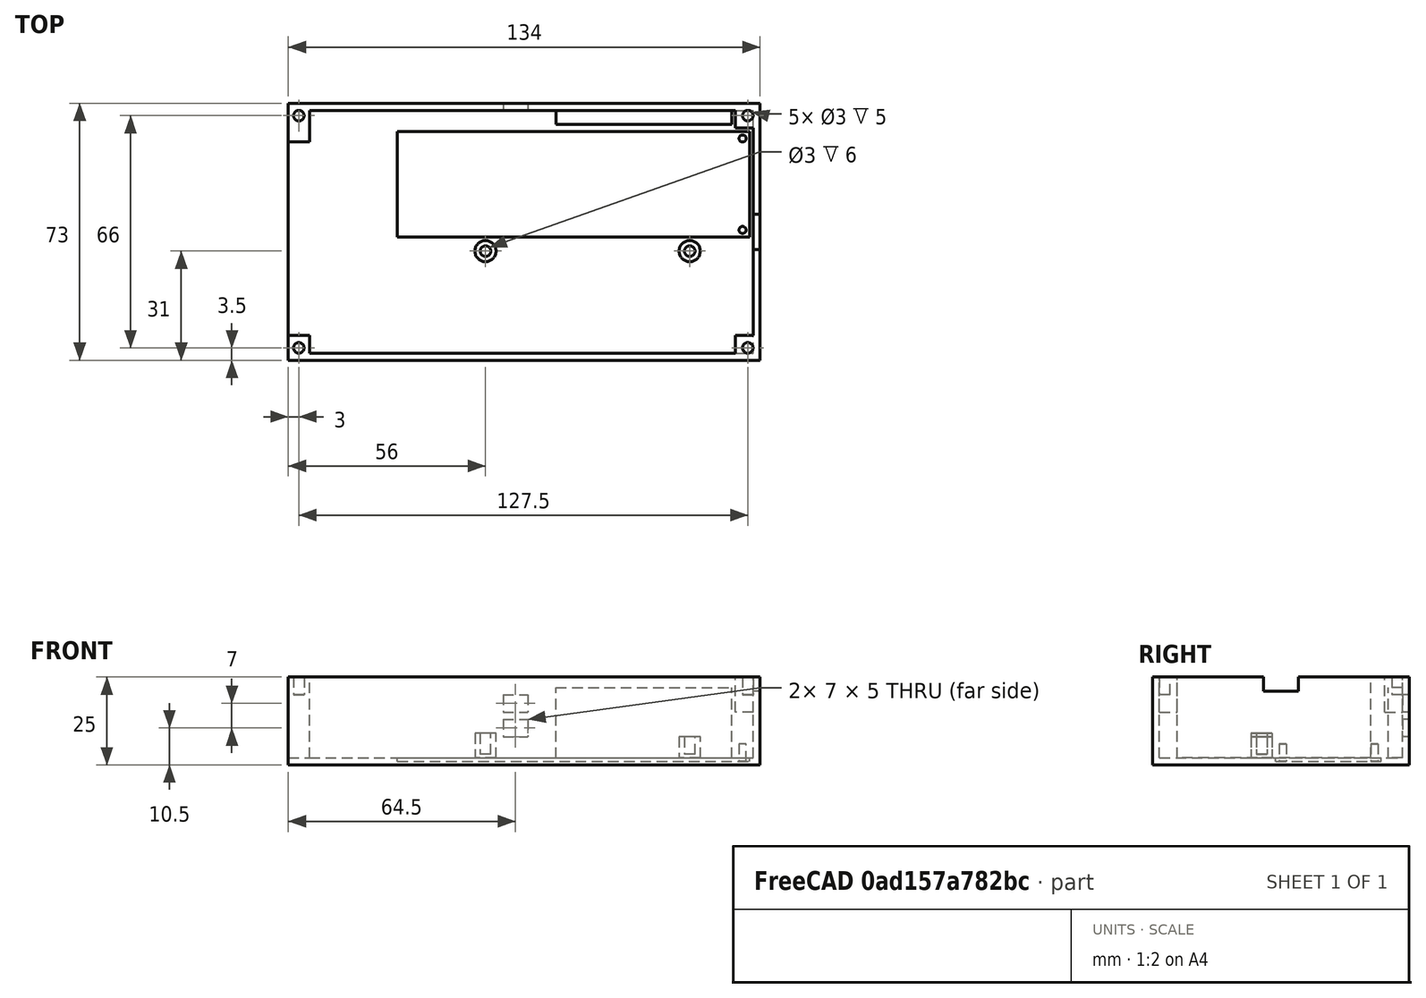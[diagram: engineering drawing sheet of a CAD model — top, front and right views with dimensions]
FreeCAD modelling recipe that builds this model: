
FCSTD DOCUMENT  (FreeCAD 1.0R39285 (Git))
Label: caseBottomV1NoFillets
License: All rights reserved
LicenseURL: https://en.wikipedia.org/wiki/All_rights_reserved
objects: PartDesign::SubtractiveBox×6, PartDesign::SubtractiveCylinder×6, PartDesign::AdditiveBox×4, PartDesign::AdditiveCylinder×4, PartDesign::Body×1
note: 61 computed .brp shape members not serialized (recipe doc carries the construction recipe); baked Part::Feature solids carry a one-line shape summary decoded from their .brp

FEATURE [PartDesign::AdditiveBox] Box  label="base"
  AttacherType = Attacher::AttachEngine3D
  Height = 25
  Length = 134
  Refine = true
  Suppressed = false
  Width = 73
FEATURE [PartDesign::SubtractiveBox] Box001  label="primaryHollow"
  AttacherType = Attacher::AttachEngine3D
  AttachmentOffset = pos=(6,2,-23) rot=(0,0,1;0rad)
  AttachmentSupport = -> [Box]
  BaseFeature = -> Box
  Height = 23
  Length = 126
  MapMode = 5
  Placement = pos=(6,2,2) rot=(0,0,1;0rad)
  Refine = true
  Suppressed = false
  Width = 69
FEATURE [PartDesign::SubtractiveBox] Box002  label="dacGap"
  AttacherType = Attacher::AttachEngine3D
  AttachmentOffset = pos=(-8,5,0) rot=(0,0,1;0rad)
  AttachmentSupport = -> [Box001]
  BaseFeature = -> Box001
  Height = 23
  Length = 10
  MapMode = 2
  Placement = pos=(-2,7,2) rot=(0,0,1;0rad)
  Refine = true
  Suppressed = false
  Width = 55
FEATURE [PartDesign::SubtractiveBox] Box003  label="batteryPCBRecess"
  AttacherType = Attacher::AttachEngine3D
  AttachmentOffset = pos=(33,28,-1) rot=(0,0,1;0rad)
  AttachmentSupport = -> [Box002]
  BaseFeature = -> Box002
  Height = 1
  Length = 100
  MapMode = 5
  Placement = pos=(31,35,1) rot=(0,0,1;0rad)
  Refine = true
  Suppressed = false
  Width = 30
FEATURE [PartDesign::AdditiveCylinder] Cylinder  label="batteryPCBSupport1"
  Angle = 360
  AttacherType = Attacher::AttachEngine3D
  AttachmentOffset = pos=(98,2,0) rot=(0,0,1;0rad)
  AttachmentSupport = -> [Box003]
  BaseFeature = -> Box003
  FirstAngle = 0
  Height = 5
  MapMode = 5
  Placement = pos=(129,37,1) rot=(0,0,1;0rad)
  Radius = 1
  Refine = true
  SecondAngle = 0
  Suppressed = false
FEATURE [PartDesign::AdditiveCylinder] Cylinder001  label="batteryPCBSupport2"
  Angle = 360
  AttacherType = Attacher::AttachEngine3D
  AttachmentOffset = pos=(98,28,0) rot=(0,0,1;0rad)
  AttachmentSupport = -> [Box003]
  BaseFeature = -> Cylinder
  FirstAngle = 0
  Height = 5
  MapMode = 2
  Placement = pos=(129,63,1) rot=(0,0,1;0rad)
  Radius = 1
  Refine = true
  SecondAngle = 0
  Suppressed = false
FEATURE [PartDesign::AdditiveCylinder] Cylinder002  label="rpiSupport1"
  Angle = 360
  AttacherType = Attacher::AttachEngine3D
  AttachmentOffset = pos=(-15,-32,-1) rot=(0,0,1;0rad)
  AttachmentSupport = -> [Cylinder001]
  BaseFeature = -> Cylinder001
  FirstAngle = 0
  Height = 7
  MapMode = 5
  Placement = pos=(114,31,1) rot=(0,0,1;0rad)
  Radius = 3
  Refine = true
  SecondAngle = 0
  Suppressed = false
FEATURE [PartDesign::SubtractiveCylinder] Cylinder003  label="rpiSupport1Hollow"
  Angle = 360
  AttacherType = Attacher::AttachEngine3D
  AttachmentOffset = pos=(0,0,1) rot=(0,0,1;0rad)
  AttachmentSupport = -> [Cylinder002]
  BaseFeature = -> Cylinder002
  FirstAngle = 0
  Height = 6
  MapMode = 5
  Placement = pos=(114,31,3) rot=(0,0,1;0rad)
  Radius = 1.5
  Refine = true
  SecondAngle = 0
  Suppressed = false
FEATURE [PartDesign::AdditiveCylinder] Cylinder004  label="rpiSupport2"
  Angle = 360
  AttacherType = Attacher::AttachEngine3D
  AttachmentOffset = pos=(-58,0,0) rot=(0,0,1;0rad)
  AttachmentSupport = -> [Cylinder003]
  BaseFeature = -> Cylinder003
  FirstAngle = 0
  Height = 7
  MapMode = 5
  Placement = pos=(56,31,2) rot=(0,0,1;0rad)
  Radius = 3
  Refine = true
  SecondAngle = 0
  Suppressed = false
FEATURE [PartDesign::SubtractiveCylinder] Cylinder005  label="rpiSupport2Hollow"
  Angle = 360
  AttacherType = Attacher::AttachEngine3D
  AttachmentOffset = pos=(0,0,-6) rot=(0,0,1;0rad)
  AttachmentSupport = -> [Cylinder004]
  BaseFeature = -> Cylinder004
  FirstAngle = 0
  Height = 6
  MapMode = 5
  Placement = pos=(56,31,3) rot=(0,0,1;0rad)
  Radius = 1.5
  Refine = true
  SecondAngle = 0
  Suppressed = false
FEATURE [PartDesign::SubtractiveBox] Box004  label="powerSwitch"
  AttacherType = Attacher::AttachEngine3D
  AttachmentOffset = pos=(5,5,-3) rot=(0,0,1;0rad)
  AttachmentSupport = -> [Cylinder005]
  BaseFeature = -> Cylinder005
  Height = 7
  Length = 7
  MapMode = 5
  Placement = pos=(61,74,8) rot=(1,0,0;1.5708rad)
  Refine = true
  Suppressed = false
  Width = 5
FEATURE [PartDesign::SubtractiveBox] Box005  label="holdSwitch"
  AttacherType = Attacher::AttachEngine3D
  AttachmentOffset = pos=(0,7,-3) rot=(0,0,1;0rad)
  AttachmentSupport = -> [Box004]
  BaseFeature = -> Box004
  Height = 5
  Length = 7
  MapMode = 5
  Placement = pos=(61,74,15) rot=(1,0,0;1.5708rad)
  Refine = true
  Suppressed = false
  Width = 5
FEATURE [PartDesign::AdditiveBox] Box006  label="clickwheelSideSupport"
  AttacherType = Attacher::AttachEngine3D
  AttachmentOffset = pos=(15,-13,0) rot=(0,0,1;0rad)
  AttachmentSupport = -> [Box005]
  BaseFeature = -> Box005
  Height = 4
  Length = 50
  MapMode = 5
  Placement = pos=(76,71,2) rot=(1,0,0;1.5708rad)
  Refine = true
  Suppressed = false
  Width = 20
FEATURE [PartDesign::SubtractiveBox] Box007  label="usbPortHollow"
  AttacherType = Attacher::AttachEngine3D
  AttachmentOffset = pos=(-23,29.5,-2) rot=(0,0,1;0rad)
  AttachmentSupport = -> [Box006]
  BaseFeature = -> Box006
  Height = 2
  Length = 4
  MapMode = 5
  Placement = pos=(134,41.5,25) rot=(0.707107,0,-0.707107;3.14159rad)
  Refine = true
  Suppressed = false
  Width = 10
FEATURE [PartDesign::SubtractiveCylinder] Cylinder006  label="topScrewHollow1"
  Angle = 360
  AttacherType = Attacher::AttachEngine3D
  AttachmentOffset = pos=(-38,131,-5) rot=(0,0,1;0rad)
  AttachmentSupport = -> [Box007]
  BaseFeature = -> Box007
  FirstAngle = 0
  Height = 5
  MapMode = 5
  Placement = pos=(3,3.5,20) rot=(0,0,1;1.5708rad)
  Radius = 1.5
  Refine = true
  SecondAngle = 0
  Suppressed = false
FEATURE [PartDesign::SubtractiveCylinder] Cylinder007  label="topScrewHollow2"
  Angle = 360
  AttacherType = Attacher::AttachEngine3D
  AttachmentOffset = pos=(66,0,-5) rot=(0,0,1;0rad)
  AttachmentSupport = -> [Cylinder006]
  BaseFeature = -> Cylinder006
  FirstAngle = 0
  Height = 5
  MapMode = 5
  Placement = pos=(3,69.5,20) rot=(0,0,1;1.5708rad)
  Radius = 1.5
  Refine = true
  SecondAngle = 0
  Suppressed = false
FEATURE [PartDesign::AdditiveBox] Box008  label="bottomScrew1"
  AttacherType = Attacher::AttachEngine3D
  AttachmentOffset = pos=(-67.5,-129,-10) rot=(0,0,1;0rad)
  AttachmentSupport = -> [Cylinder007]
  BaseFeature = -> Cylinder007
  Height = 10
  Length = 5
  MapMode = 5
  Placement = pos=(132,2,15) rot=(0,0,1;1.5708rad)
  Refine = true
  Suppressed = false
  Width = 5
FEATURE [PartDesign::AdditiveBox] Box009  label="bottomScrew2"
  AttacherType = Attacher::AttachEngine3D
  AttachmentOffset = pos=(64,0,-10) rot=(0,0,1;0rad)
  AttachmentSupport = -> [Box008]
  BaseFeature = -> Box008
  Height = 10
  Length = 5
  MapMode = 5
  Placement = pos=(132,66,15) rot=(0,0,1;1.5708rad)
  Refine = true
  Suppressed = false
  Width = 5
FEATURE [PartDesign::SubtractiveCylinder] Cylinder008  label="bottomScrewHollow2"
  Angle = 360
  AttacherType = Attacher::AttachEngine3D
  AttachmentOffset = pos=(3.5,1.5,-5) rot=(0,0,1;0rad)
  AttachmentSupport = -> [Box009]
  BaseFeature = -> Box009
  FirstAngle = 0
  Height = 5
  MapMode = 5
  Placement = pos=(130.5,69.5,20) rot=(0,0,1;1.5708rad)
  Radius = 1.5
  Refine = true
  SecondAngle = 0
  Suppressed = false
FEATURE [PartDesign::SubtractiveCylinder] Cylinder009  label="BottomScrewHollow1"
  Angle = 360
  AttacherType = Attacher::AttachEngine3D
  AttachmentOffset = pos=(-66,0,-5) rot=(0,0,1;0rad)
  AttachmentSupport = -> [Cylinder008]
  BaseFeature = -> Cylinder008
  FirstAngle = 0
  Height = 5
  MapMode = 5
  Placement = pos=(130.5,3.5,20) rot=(0,0,1;1.5708rad)
  Radius = 1.5
  Refine = true
  SecondAngle = 0
  Suppressed = false
FEATURE [PartDesign::Body] Body
  AllowCompound = false
  Group = -> [Box,Box001,Box002,Box003,Cylinder,Cylinder001,Cylinder002,Cylinder003,Cylinder004,Cylinder005,Box004,Box005,Box006,Box007,Cylinder006,Cylinder007,Box008,Box009,Cylinder008,Cylinder009]
  Origin = -> Origin
  Tip = -> Cylinder009
